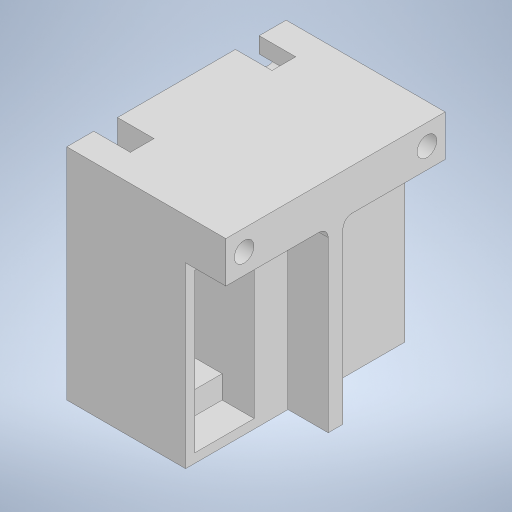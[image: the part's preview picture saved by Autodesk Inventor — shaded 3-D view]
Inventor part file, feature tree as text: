
AUTODESK INVENTOR PART (.ipt)
format: ipt  version: 2023 (Build 270158000, 158)  size: 337,920 bytes
history: native  units: in
note: dims shown in document units (in); Inventor stores cm internally (conversion verified against a paired STEP export)
features: extrude x9, sketch x8, projected_geometry x7, mirror x3
ambient origin geometry x8: Origin, YZ Plane, XZ Plane, XY Plane, X Axis, Y Axis, Z Axis, Center Point
bodies: Solid1 (feature_tree)
feature tree (27):
  extrude  "Extrusion1"  Depth=3.0in
  extrude  "Extrusion2"  Depth=1.5in
  extrude  "Extrusion3"  Depth=1.5625in TaperAngle=0.0deg
  extrude  "Extrusion4"  Depth=0.4375in TaperAngle=0.0deg
  mirror  "Mirror1"
  extrude  "Extrusion5"  Depth=0.1in
  extrude  "Extrusion6"  Depth=0.55in TaperAngle=0.0deg
  extrude  "Extrusion7"  Depth=2.4375in TaperAngle=0.0deg
  mirror  "Mirror2"
  extrude  "Extrusion8"  Depth=0.125in
  mirror  "Mirror3"
  extrude  "Extrusion10"  Depth=0.5625in TaperAngle=0.0deg
  sketch  "Sketch1"  dims[d0=3.0in d1=3.0in]
  sketch  "Sketch2"  dims[d2=1.5in d3=1.5in]
  sketch  "Sketch3"  dims[d4=1.625in d5=0.0in d13=1.5625in d14=0.0in]
  sketch  "Sketch4"  dims[d24=0.4375in d25=0.0in d34=1.5in d35=0.0in]
  projected_geometry  "Projected Loop4"
  projected_geometry  "Projected Loop5"
  sketch  "Sketch6"  dims[d36=0.2in d39=0.1in]
  sketch  "Sketch7"  dims[d40=0.125in d41=0.55in d42=0.0in]
  projected_geometry  "Projected Loop6"
  sketch  "Sketch8"  dims[d43=2.4375in d44=2.4375in d45=1.0in d46=0.0in]
  projected_geometry  "Projected Loop9"
  projected_geometry  "Projected Loop10"
  projected_geometry  "Projected Loop11"
  sketch  "Sketch11"  dims[d49=0.375in d50=0.125in d51=1.0in d52=0.0in d53=0.1902in d54=0.375in d55=0.0in d64=0.8125in d65=1.75in d66=0.125in d67=0.4375in d68=0.3125in d69=0.8125in d70=0.8125in d71=0.8125in d72=0.1in d73=0.325in d74=0.5in d75=0.8125in d76=0.4062in d77=2.5in d78=3.0in d79=1.25in d80=0.5625in d81=0.2812in d82=0.2812in d83=0.27in d84=0.27in d85=0.0in d86=0.0in]
  projected_geometry  "Projected Loop12"
